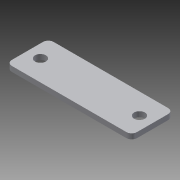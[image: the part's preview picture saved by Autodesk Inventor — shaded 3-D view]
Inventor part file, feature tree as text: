
AUTODESK INVENTOR PART (.ipt)
format: ipt  version: 2013 (Build 170138000, 138)  size: 85,504 bytes
history: native  units: in
note: dims shown in document units (in); Inventor stores cm internally (conversion verified against a paired STEP export)
features: extrude x1, fillet x1, sketch x1
ambient origin geometry x8: Origin, YZ Plane, XZ Plane, XY Plane, X Axis, Y Axis, Z Axis, Center Point
bodies: Solid1 (feature_tree)
feature tree (3):
  extrude  "Extrusion1"  Depth=0.26in
  fillet  "Fillet1"  Radius=2.375in
  sketch  "Sketch1"  dims[d0=3.0in d1=0.26in d2=2.375in d3=1.0in d4=0.125in d5=0.0in d6=0.125in]
